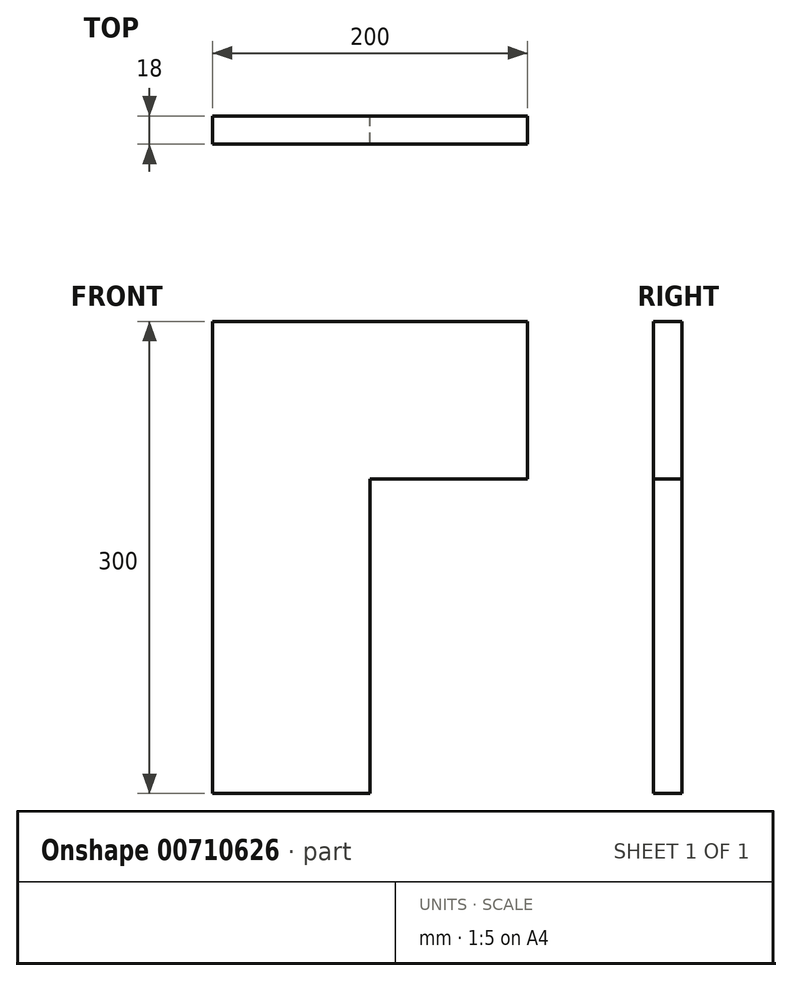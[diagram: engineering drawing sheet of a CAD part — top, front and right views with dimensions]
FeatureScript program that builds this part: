
annotation { "Feature Type Name" : "Feature", "Feature Type Description" : "" }
export const myFeature = defineFeature(function(context is Context, id is Id, definition is map)
    precondition{}
    {
        {
            var Q0;
            Q0=qCreatedBy(makeId("Front.planeOp"),FACE);
            var sketch = newSketch(context, id + "F0", { "sketchPlane" : qUnion([Q0])});
            skLineSegment(sketch, "E0.bottom", {"start": v(0, 0) * mm, "end": v(100, 0) * mm});
            skLineSegment(sketch, "E0.top", {"start": v(0, 300) * mm, "end": v(100, 300) * mm});
            skLineSegment(sketch, "E0.left", {"start": v(0, 0) * mm, "end": v(0, 300) * mm});
            skLineSegment(sketch, "E0.right", {"start": v(100, 0) * mm, "end": v(100, 200) * mm});
            skLineSegment(sketch, "E1.bottom", {"start": v(100, 300) * mm, "end": v(200, 300) * mm});
            skLineSegment(sketch, "E1.top", {"start": v(100, 200) * mm, "end": v(200, 200) * mm});
            skLineSegment(sketch, "E1.right", {"start": v(200, 300) * mm, "end": v(200, 200) * mm});
            skSolve(sketch);
        }
        {
            var Q0;
            Q0=makeQuery(id+"F0.imprint","IMPRINT",FACE,{"disambiguationData":[TD([[makeQuery(id+"F0.imprint","IMPRINT",EDGE,{"derivedFrom":sQuery(id+"F0.wireOp",EDGE,"E0.bottom")}),1.0]])]});
            extrude(context, id + "F1", {"entities" : qUnion([Q0]), "depth" : 18 * mm, "offsetDistance" : 25 * mm});
        }
    });
